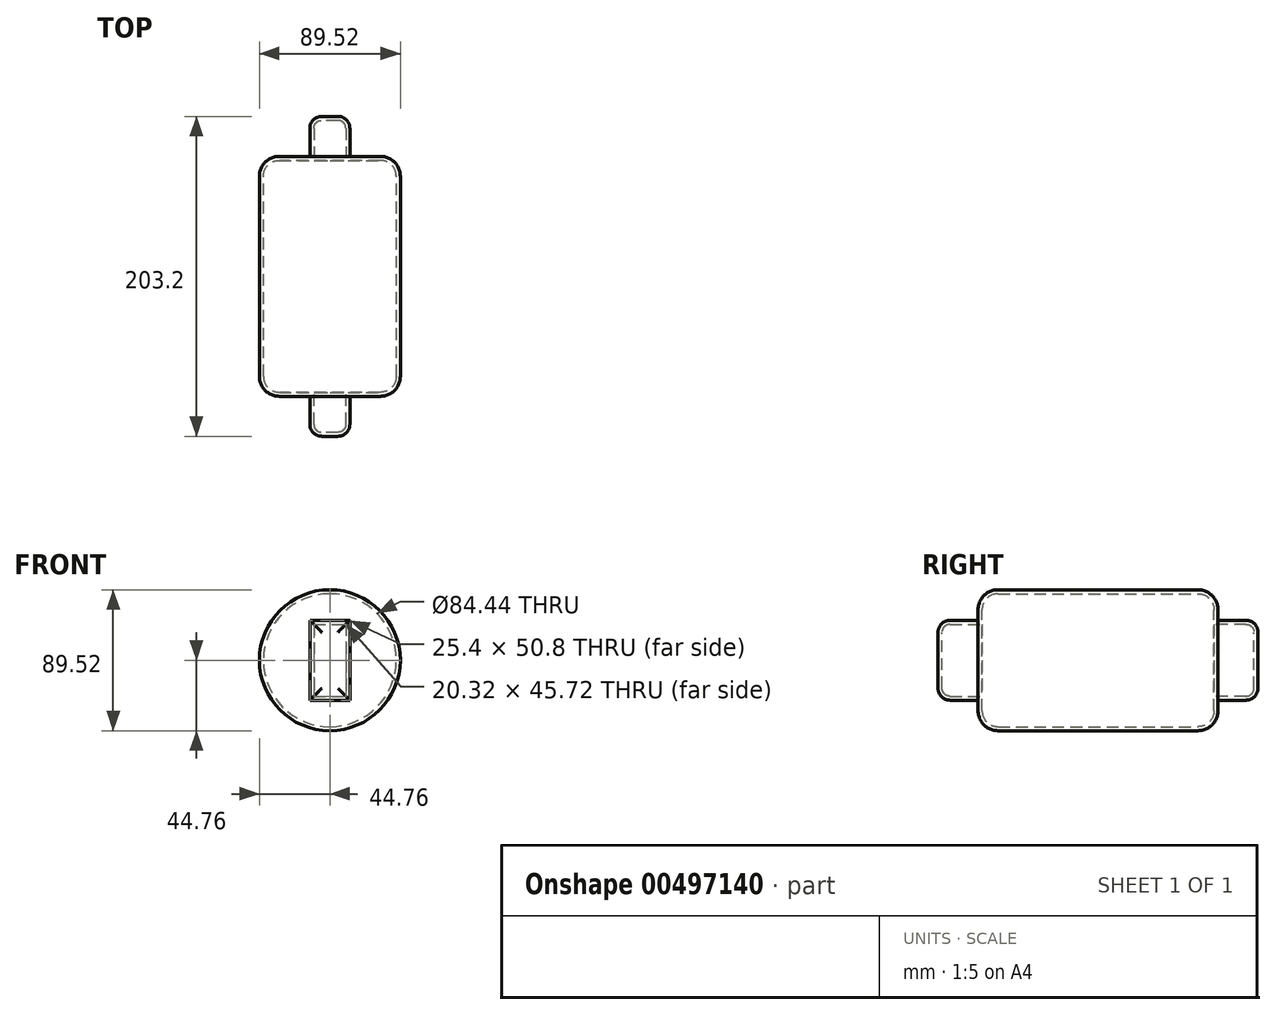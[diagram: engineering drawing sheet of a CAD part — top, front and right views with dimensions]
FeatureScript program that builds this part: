
annotation { "Feature Type Name" : "Feature", "Feature Type Description" : "" }
export const myFeature = defineFeature(function(context is Context, id is Id, definition is map)
    precondition{}
    {
        {
            var Q0;
            Q0=qCreatedBy(makeId("Front.planeOp"),FACE);
            var sketch = newSketch(context, id + "F0", { "sketchPlane" : qUnion([Q0])});
            skCircle(sketch, "E0", {"center": v(0, 0) * mm, "radius": 44.76 * mm});
            skSolve(sketch);
        }
        {
            var Q0;
            Q0 = qSketchRegion(id + "F0", true);
            extrude(context, id + "F1", {"entities" : qUnion([Q0]), "offsetDistance" : 25.4 * mm, "depth" : 76.2 * mm});
        }
        {
            var Q0;
            Q0 = qSketchRegion(id + "F0", true);
            extrude(context, id + "F2", {"entities" : qUnion([Q0]), "operationType" : NewBodyOperationType.ADD, "depth" : 25.4 * mm, "offsetDistance" : 25.4 * mm});
        }
        {
            var Q0;
            Q0=makeQuery(id+"F1.opExtrude","CAP_FACE",FACE,{"disambiguationData":[OSD([sQuery(id+"F0.wireOp",EDGE,"E0")])],"isStart":true});
            var sketch = newSketch(context, id + "F3", { "sketchPlane" : qUnion([Q0])});
            skLineSegment(sketch, "E1.bottom", {"start": v(12.7, 25.4) * mm, "end": v(-12.7, 25.4) * mm});
            skLineSegment(sketch, "E1.top", {"start": v(12.7, -25.4) * mm, "end": v(-12.7, -25.4) * mm});
            skLineSegment(sketch, "E1.left", {"start": v(12.7, 25.4) * mm, "end": v(12.7, -25.4) * mm});
            skLineSegment(sketch, "E1.right", {"start": v(-12.7, 25.4) * mm, "end": v(-12.7, -25.4) * mm});
            skPoint(sketch, "E1.middle", {"position": v(0, 0) * mm});
            skSolve(sketch);
        }
        {
            var Q0;
            Q0=makeQuery(id+"F1.opExtrude","CAP_EDGE",EDGE,{"disambiguationData":[OSD([sQuery(id+"F0.wireOp",EDGE,"E0")])],"isStart":true});
            fillet(context, id + "F4", {"entities" : qUnion([Q0]), "tangentPropagation" : true, "radius" : 12.7 * mm, "defaultsChanged" : true, "vertexSettings" : [], "allowEdgeOverflow" : false});
        }
        {
            var Q0;
            Q0 = qSketchRegion(id + "F3", true);
            extrude(context, id + "F5", {"entities" : qUnion([Q0]), "operationType" : NewBodyOperationType.ADD, "depth" : 25.4 * mm, "offsetDistance" : 25.4 * mm});
        }
        {
            var Q0;
            Q0=makeQuery(id+"F5.opExtrude","CAP_FACE",FACE,{"disambiguationData":[OSD([sQuery(id+"F3.wireOp",EDGE,"E1.bottom"),sQuery(id+"F3.wireOp",EDGE,"E1.top"),sQuery(id+"F3.wireOp",EDGE,"E1.left"),sQuery(id+"F3.wireOp",EDGE,"E1.right")])],"isStart":false});
            fillet(context, id + "F6", {"entities" : qUnion([Q0]), "tangentPropagation" : true, "radius" : 7.62 * mm, "defaultsChanged" : true, "vertexSettings" : [], "allowEdgeOverflow" : false});
        }
        {
            var Q0;
            Q0=makeQuery(id+"F1.opExtrude","CAP_FACE",FACE,{"disambiguationData":[OSD([sQuery(id+"F0.wireOp",EDGE,"E0")])],"isStart":false});
            shell(context, id + "F7", {"entities" : qUnion([Q0]), "thickness" : 2.54 * mm});
        }
        {
            var Q0;
            Q0=makeQuery(id+"F1.opExtrude","SWEPT_BODY",BODY,{"disambiguationData":[OSD([sQuery(id+"F0.wireOp",EDGE,"E0")])]});
            var Q1;
            Q1=makeQuery(id+"F1.opExtrude","CAP_FACE",FACE,{"disambiguationData":[OSD([sQuery(id+"F0.wireOp",EDGE,"E0")])],"isStart":false});
            mirror(context, id + "F8", {"operationType" : NewBodyOperationType.ADD, "entities" : qUnion([Q0]), "mirrorPlane" : qUnion([Q1])});
        }
    });
